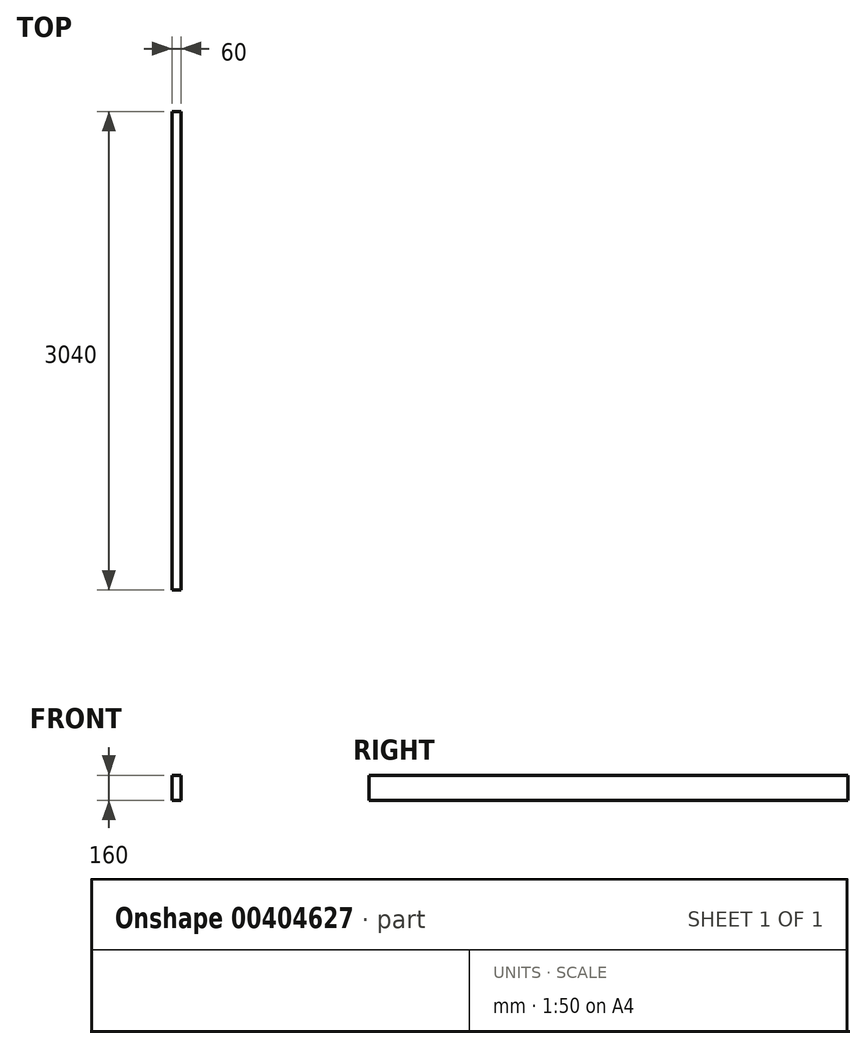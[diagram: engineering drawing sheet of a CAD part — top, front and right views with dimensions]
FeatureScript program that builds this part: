
annotation { "Feature Type Name" : "Feature", "Feature Type Description" : "" }
export const myFeature = defineFeature(function(context is Context, id is Id, definition is map)
    precondition{}
    {
        {
            var Q0;
            Q0=qCreatedBy(makeId("Front.planeOp"),FACE);
            var sketch = newSketch(context, id + "F0", { "sketchPlane" : qUnion([Q0])});
            skLineSegment(sketch, "E0.bottom", {"start": v(-30, 80) * mm, "end": v(30, 80) * mm});
            skLineSegment(sketch, "E0.top", {"start": v(-30, -80) * mm, "end": v(30, -80) * mm});
            skLineSegment(sketch, "E0.left", {"start": v(-30, 80) * mm, "end": v(-30, -80) * mm});
            skLineSegment(sketch, "E0.right", {"start": v(30, 80) * mm, "end": v(30, -80) * mm});
            skSolve(sketch);
        }
        {
            var Q0;
            Q0 = qSketchRegion(id + "F0", true);
            extrude(context, id + "F1", {"entities" : qUnion([Q0]), "depth" : 3040 * mm});
        }
    });
